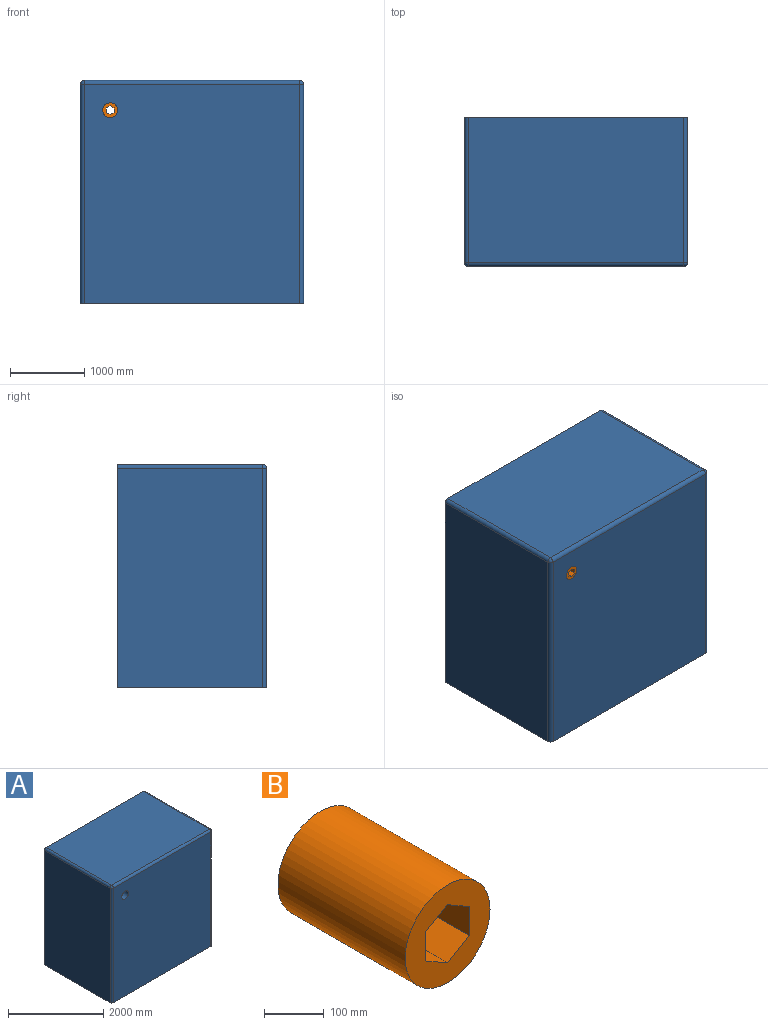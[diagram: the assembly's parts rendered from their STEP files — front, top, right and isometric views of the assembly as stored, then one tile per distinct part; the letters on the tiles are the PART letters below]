
ASSEMBLY  parts=2 mates=1
PART A: 19 faces, bbox 3000x2000x3000 mm
  f0: plane 2950x1950mm, normal (1,0,0), area 5752500mm2, adj f3,f5,f16,f18
  f1: plane 2900x1950mm, normal (0,0,1), area 5655000mm2, adj f5,f12,f13,f18
  f2: plane 2950x1950mm, normal (-1,0,0), area 5752500mm2, adj f3,f5,f12,f15
  f3: plane 3000x2000mm, normal (0,0,-1), area 5998927mm2, adj f0,f2,f4,f5,f15,f16
  f4: plane 2950x2900mm, normal (0,-1,0), area 8523584.1mm2, adj f3,f11,f13,f15,f16
  f5: plane 3000x3000mm, normal (0,1,0), area 2748927mm2, adj f0,f1,f2,f3,f6,f7,f8,f9
  f6: plane 2500x1800mm, normal (1,0,0), area 4500000mm2, adj f5,f7,f9,f10
  f7: plane 2500x1800mm, normal (0,0,-1), area 4500000mm2, adj f5,f6,f8,f10
  f8: plane 2500x1800mm, normal (-1,0,0), area 4500000mm2, adj f5,f7,f9,f10
  f9: plane 2500x1800mm, normal (0,0,1), area 4500000mm2, adj f5,f6,f8,f10
  f10: plane 2500x2500mm, normal (0,1,0), area 6218584.1mm2, adj f6,f7,f8,f9,f11
  f11: cylinder r=100mm len=200mm, axis (0,-1,0), area 125663.7mm2, adj f4,f10
  f12: cylinder r=50mm len=1950mm, axis (0,-1,0), area 153152.6mm2, adj f1,f2,f5,f14
  f13: cylinder r=50mm len=2900mm, axis (1,0,0), area 227765.5mm2, adj f1,f4,f14,f17
  f14: sphere r=50mm, area 3927mm2, adj f12,f13,f15
  f15: cylinder r=50mm len=2950mm, axis (0,0,1), area 231692.5mm2, adj f2,f3,f4,f14
  f16: cylinder r=50mm len=2950mm, axis (0,0,-1), area 231692.5mm2, adj f0,f3,f4,f17
  f17: sphere r=50mm, area 3927mm2, adj f13,f16,f18
  f18: cylinder r=50mm len=1950mm, axis (0,1,0), area 153152.6mm2, adj f0,f1,f5,f17
PART B: 9 faces, bbox 200x300x200 mm
  f0: plane 200x200mm, normal (0,-1,0), area 22229.4mm2, adj f2,f3,f4,f5,f6,f7,f8
  f1: plane 200x200mm, normal (0,1,0), area 22229.4mm2, adj f2,f3,f4,f5,f6,f7,f8
  f2: cylinder r=100mm len=300mm, axis (0,1,0), area 188495.6mm2, adj f0,f1
  f3: plane 300x51.5mm, normal (-0.5,0,-0.87), area 17839mm2, adj f0,f1,f4,f8
  f4: plane 300x51.5mm, normal (0.5,0,-0.87), area 17839mm2, adj f0,f1,f3,f5
  f5: plane 300x59.46mm, normal (1,0,0), area 17839mm2, adj f0,f1,f4,f6
  f6: plane 300x51.5mm, normal (0.5,0,0.87), area 17839mm2, adj f0,f1,f5,f7
  f7: plane 300x51.5mm, normal (-0.5,0,0.87), area 17839mm2, adj f0,f1,f6,f8
  f8: plane 300x59.46mm, normal (-1,0,0), area 17839mm2, adj f0,f1,f3,f7
PLACE A t=(-770.93,150.02,298.72)mm fixed
PLACE B t=(-1870.93,-1549.98,1398.72)mm
MATE cylindrical B.f2 <-> A.f11  axis (0,-1,0) through (-1870.93,-1849.98,1398.72)mm
